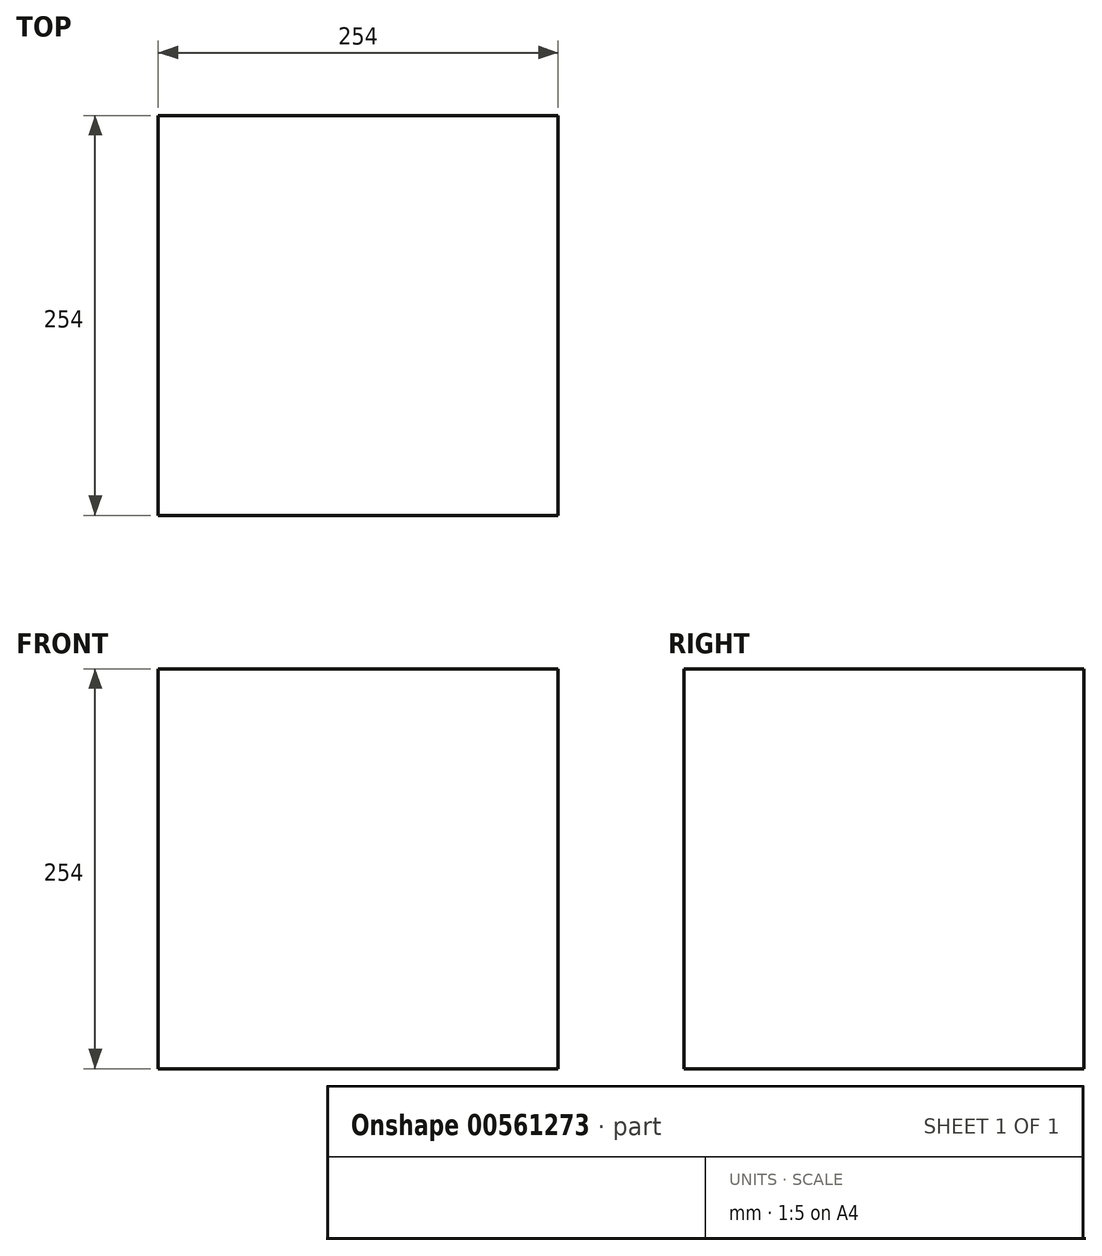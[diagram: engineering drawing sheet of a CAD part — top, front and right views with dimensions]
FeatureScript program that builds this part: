
annotation { "Feature Type Name" : "Feature", "Feature Type Description" : "" }
export const myFeature = defineFeature(function(context is Context, id is Id, definition is map)
    precondition{}
    {
        {
            var Q0;
            Q0=qCreatedBy(makeId("Front.planeOp"),FACE);
            var sketch = newSketch(context, id + "F0", { "sketchPlane" : qUnion([Q0])});
            skLineSegment(sketch, "E0.bottom", {"start": v(127, 127) * mm, "end": v(-127, 127) * mm});
            skLineSegment(sketch, "E0.top", {"start": v(127, -127) * mm, "end": v(-127, -127) * mm});
            skLineSegment(sketch, "E0.left", {"start": v(127, 127) * mm, "end": v(127, -127) * mm});
            skLineSegment(sketch, "E0.right", {"start": v(-127, 127) * mm, "end": v(-127, -127) * mm});
            skPoint(sketch, "E0.middle", {"position": v(0, 0) * mm});
            skSolve(sketch);
        }
        {
            var Q0;
            Q0=makeQuery(id+"F0.imprint","IMPRINT",FACE,{"disambiguationData":[TD([[makeQuery(id+"F0.imprint","IMPRINT",EDGE,{"derivedFrom":sQuery(id+"F0.wireOp",EDGE,"E0.bottom")}),1.0]])]});
            extrude(context, id + "F1", {"entities" : qUnion([Q0]), "depth" : 127 * mm, "offsetDistance" : 25.4 * mm, "hasSecondDirection" : true, "secondDirectionOppositeDirection" : true, "secondDirectionDepth" : 127 * mm});
        }
    });
